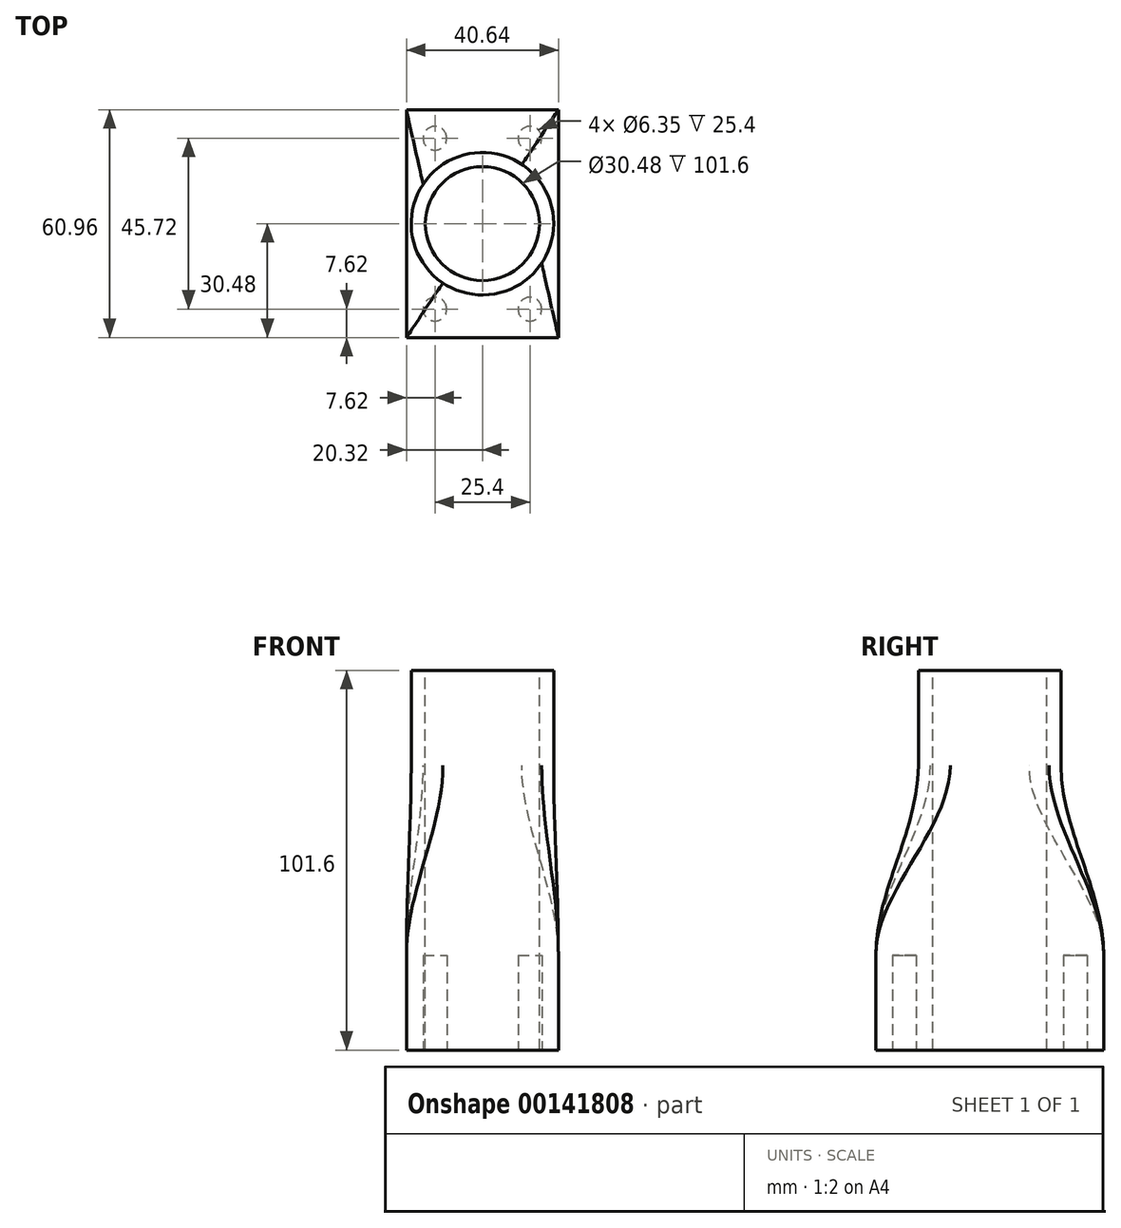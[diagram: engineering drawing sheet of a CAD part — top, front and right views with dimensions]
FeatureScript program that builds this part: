
annotation { "Feature Type Name" : "Feature", "Feature Type Description" : "" }
export const myFeature = defineFeature(function(context is Context, id is Id, definition is map)
    precondition{}
    {
        {
            var Q0;
            Q0=qCreatedBy(makeId("Top.planeOp"),FACE);
            var sketch = newSketch(context, id + "F0", { "sketchPlane" : qUnion([Q0])});
            skLineSegment(sketch, "E0.bottom", {"start": v(20.32, 30.48) * mm, "end": v(-20.32, 30.48) * mm});
            skLineSegment(sketch, "E0.top", {"start": v(20.32, -30.48) * mm, "end": v(-20.32, -30.48) * mm});
            skLineSegment(sketch, "E0.left", {"start": v(20.32, 30.48) * mm, "end": v(20.32, -30.48) * mm});
            skLineSegment(sketch, "E0.right", {"start": v(-20.32, 30.48) * mm, "end": v(-20.32, -30.48) * mm});
            skPoint(sketch, "E0.middle", {"position": v(0, 0) * mm});
            skSolve(sketch);
        }
        {
            var Q0;
            Q0=qCreatedBy(makeId("Top.planeOp"),FACE);
            cPlane(context, id + "F1", {"entities" : qUnion([Q0]), "cplaneType" : CPlaneType.OFFSET, "offset" : 50.8 * mm, "width" : 152.4 * mm, "height" : 152.4 * mm});
        }
        {
            var Q0;
            Q0=qCreatedBy(id+"F1.planeOp",FACE);
            var sketch = newSketch(context, id + "F2", { "sketchPlane" : qUnion([Q0])});
            skCircle(sketch, "E1", {"center": v(0, 0) * mm, "radius": 19.05 * mm});
            skSolve(sketch);
        }
        {
            var Q0;
            Q0=makeQuery(id+"F2.imprint","IMPRINT",FACE,{"disambiguationData":[TD([[makeQuery(id+"F2.imprint","IMPRINT",EDGE,{"derivedFrom":sQuery(id+"F2.wireOp",EDGE,"E1")}),1.0]])]});
            extrude(context, id + "F3", {"entities" : qUnion([Q0]), "depth" : 25.4 * mm});
        }
        {
            var Q0;
            Q0=makeQuery(id+"F0.imprint","IMPRINT",FACE,{"disambiguationData":[TD([[makeQuery(id+"F0.imprint","IMPRINT",EDGE,{"derivedFrom":sQuery(id+"F0.wireOp",EDGE,"E0.bottom")}),1.0]])]});
            extrude(context, id + "F4", {"entities" : qUnion([Q0]), "oppositeDirection" : true, "depth" : 25.4 * mm});
        }
        {
            var Q1;
            Q1=makeQuery(id+"F4.opExtrude","CAP_FACE",FACE,{"disambiguationData":[OSD([sQuery(id+"F0.wireOp",EDGE,"E0.bottom"),sQuery(id+"F0.wireOp",EDGE,"E0.top"),sQuery(id+"F0.wireOp",EDGE,"E0.left"),sQuery(id+"F0.wireOp",EDGE,"E0.right")])],"isStart":true});
            var Q2;
            Q2=makeQuery(id+"F3.opExtrude","CAP_FACE",FACE,{"disambiguationData":[OSD([sQuery(id+"F2.wireOp",EDGE,"E1")])],"isStart":true});
            loft(context, id + "F5", {"operationType" : NewBodyOperationType.ADD, "startCondition" : LoftEndDerivativeType.MATCH_TANGENT, "startMagnitude" : 1, "endCondition" : LoftEndDerivativeType.MATCH_TANGENT, "endMagnitude" : 1, "sheetProfilesArray" : [{ "sheetProfileEntities" : qUnion([Q1]) }, { "sheetProfileEntities" : qUnion([Q2]) }]});
        }
        {
            var Q0;
            Q0=makeQuery(id+"F3.opExtrude","CAP_FACE",FACE,{"disambiguationData":[OSD([sQuery(id+"F2.wireOp",EDGE,"E1")])],"isStart":false});
            var sketch = newSketch(context, id + "F6", { "sketchPlane" : qUnion([Q0])});
            skCircle(sketch, "E2", {"center": v(0, 0) * mm, "radius": 15.24 * mm});
            skSolve(sketch);
        }
        {
            var Q0;
            Q0=makeQuery(id+"F6.imprint","IMPRINT",FACE,{"disambiguationData":[TD([[makeQuery(id+"F6.imprint","IMPRINT",EDGE,{"derivedFrom":sQuery(id+"F6.wireOp",EDGE,"E2")}),1.0]])]});
            extrude(context, id + "F7", {"entities" : qUnion([Q0]), "operationType" : NewBodyOperationType.REMOVE, "endBound" : BoundingType.THROUGH_ALL, "oppositeDirection" : true, "depth" : 13.4 * mm});
        }
        {
            var Q0;
            Q0=makeQuery(id+"F4.opExtrude","CAP_FACE",FACE,{"disambiguationData":[OSD([sQuery(id+"F0.wireOp",EDGE,"E0.bottom"),sQuery(id+"F0.wireOp",EDGE,"E0.top"),sQuery(id+"F0.wireOp",EDGE,"E0.left"),sQuery(id+"F0.wireOp",EDGE,"E0.right")])],"isStart":false});
            var sketch = newSketch(context, id + "F8", { "sketchPlane" : qUnion([Q0])});
            skCircle(sketch, "E3", {"center": v(-12.7, 22.86) * mm, "radius": 3.18 * mm});
            skCircle(sketch, "E4.MirrorC", {"center": v(12.7, 22.86) * mm, "radius": 3.18 * mm});
            skCircle(sketch, "E5.MirrorC", {"center": v(-12.7, -22.86) * mm, "radius": 3.18 * mm});
            skCircle(sketch, "E6.MirrorC", {"center": v(12.7, -22.86) * mm, "radius": 3.18 * mm});
            skSolve(sketch);
        }
        {
            var Q0;
            Q0 = qSketchRegion(id + "F8", true);
            extrude(context, id + "F9", {"entities" : qUnion([Q0]), "operationType" : NewBodyOperationType.REMOVE, "oppositeDirection" : true, "depth" : 25.4 * mm});
        }
    });
